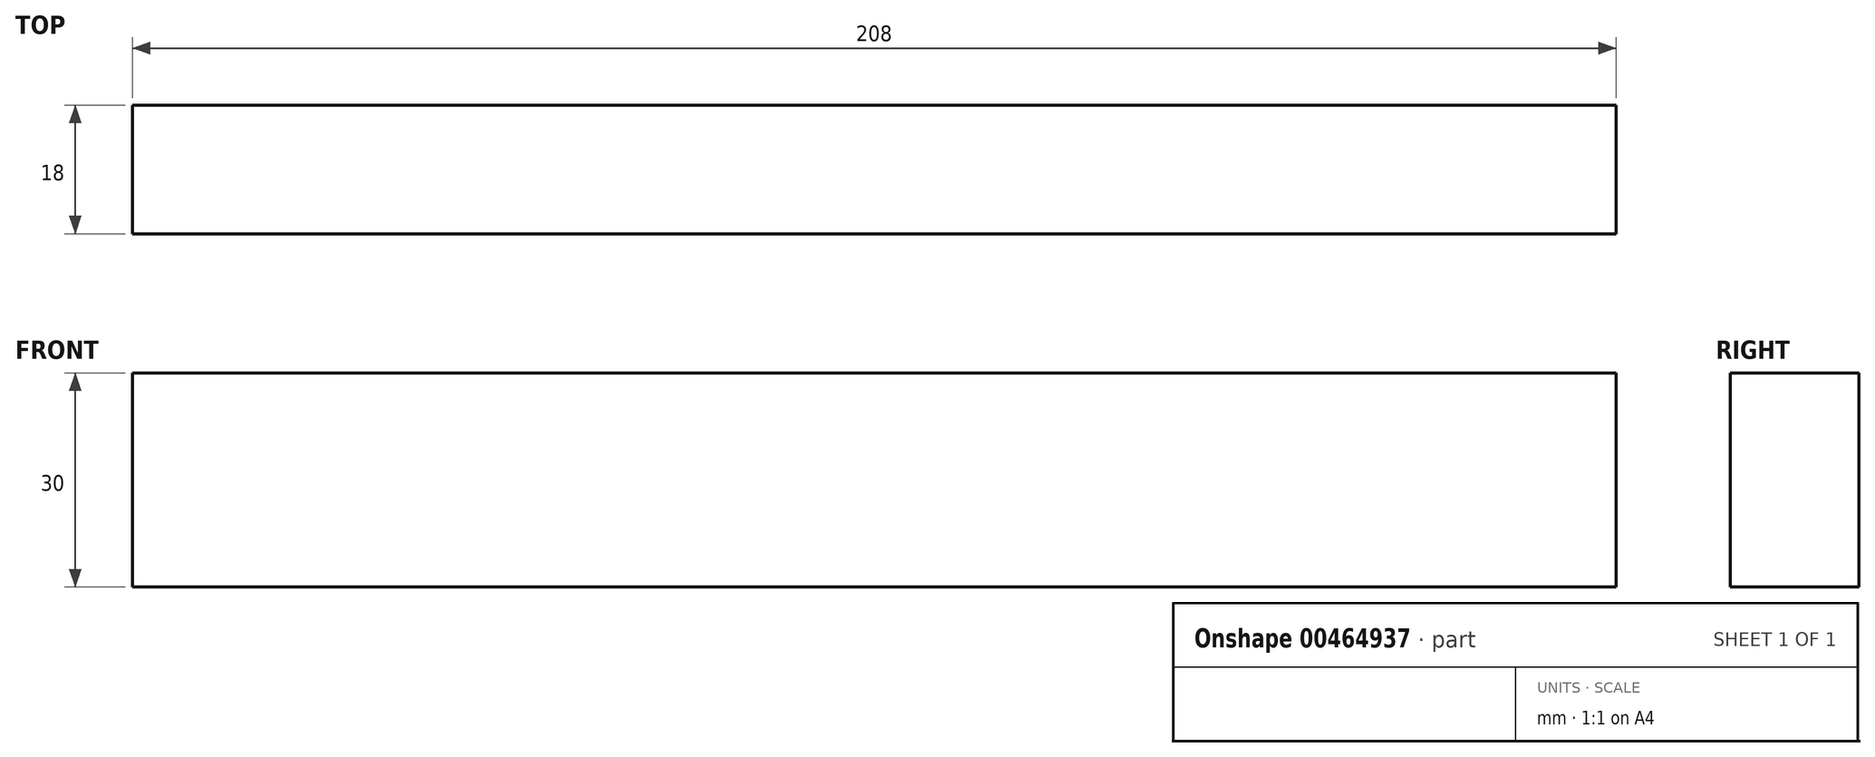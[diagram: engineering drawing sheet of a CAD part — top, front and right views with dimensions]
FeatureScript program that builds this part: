
annotation { "Feature Type Name" : "Feature", "Feature Type Description" : "" }
export const myFeature = defineFeature(function(context is Context, id is Id, definition is map)
    precondition{}
    {
        {
            var Q0;
            Q0=qCreatedBy(makeId("Right.planeOp"),FACE);
            var sketch = newSketch(context, id + "F0", { "sketchPlane" : qUnion([Q0])});
            skLineSegment(sketch, "E0.bottom", {"start": v(-9, 15) * mm, "end": v(9, 15) * mm});
            skLineSegment(sketch, "E0.top", {"start": v(-9, -15) * mm, "end": v(9, -15) * mm});
            skLineSegment(sketch, "E0.left", {"start": v(-9, 15) * mm, "end": v(-9, -15) * mm});
            skLineSegment(sketch, "E0.right", {"start": v(9, 15) * mm, "end": v(9, -15) * mm});
            skPoint(sketch, "E0.middle", {"position": v(0, 0) * mm});
            skSolve(sketch);
        }
        {
            var Q0;
            Q0=makeQuery(id+"F0.imprint","IMPRINT",FACE,{"disambiguationData":[TD([[makeQuery(id+"F0.imprint","IMPRINT",EDGE,{"derivedFrom":sQuery(id+"F0.wireOp",EDGE,"E0.bottom")}),-1.0]])]});
            extrude(context, id + "F1", {"entities" : qUnion([Q0]), "endBound" : BoundingType.SYMMETRIC, "depth" : (184 + 24) * mm, "offsetDistance" : 25 * mm});
        }
    });
